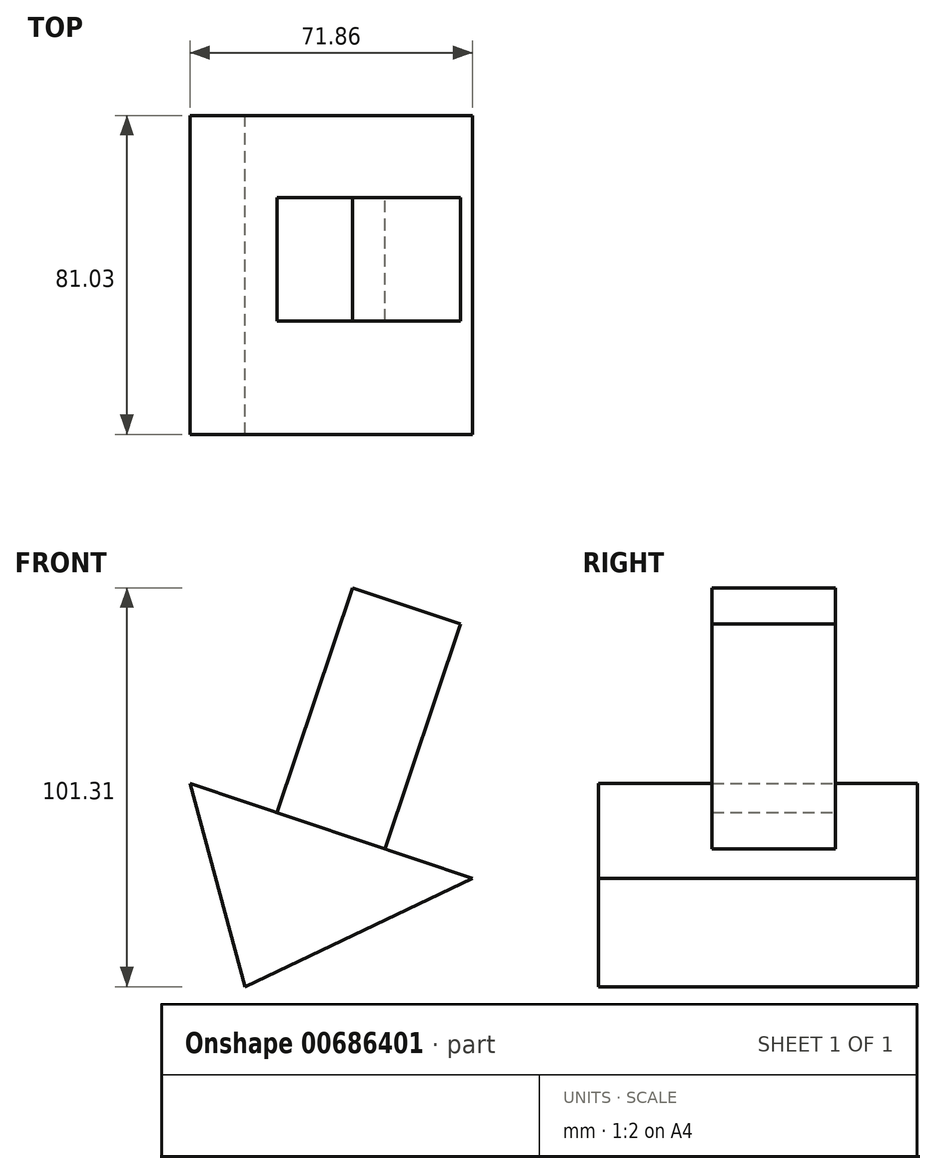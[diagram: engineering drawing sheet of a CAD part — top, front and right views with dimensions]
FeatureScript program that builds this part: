
annotation { "Feature Type Name" : "Feature", "Feature Type Description" : "" }
export const myFeature = defineFeature(function(context is Context, id is Id, definition is map)
    precondition{}
    {
        {
            var Q0;
            Q0=qCreatedBy(makeId("Front.planeOp"),FACE);
            var sketch = newSketch(context, id + "F0", { "sketchPlane" : qUnion([Q0])});
            skLineSegment(sketch, "E0", {"start": v(1.69, 0) * mm, "end": v(59.56, 27.56) * mm});
            skLineSegment(sketch, "E1", {"start": v(59.56, 27.56) * mm, "end": v(-12.3, 51.67) * mm});
            skLineSegment(sketch, "E2", {"start": v(-12.3, 51.67) * mm, "end": v(1.69, 0) * mm});
            skSolve(sketch);
        }
        {
            var Q0;
            Q0=makeQuery(id+"F0.imprint","IMPRINT",FACE,{"disambiguationData":[TD([[makeQuery(id+"F0.imprint","IMPRINT",EDGE,{"derivedFrom":sQuery(id+"F0.wireOp",EDGE,"E0")}),1.0]])]});
            extrude(context, id + "F1", {"entities" : qUnion([Q0]), "depth" : 81.03 * mm, "offsetDistance" : 25.4 * mm});
        }
        {
            var Q0;
            Q0=makeQuery(id+"F1.opExtrude","SWEPT_FACE",FACE,{"disambiguationData":[OSD([sQuery(id+"F0.wireOp",EDGE,"E1")])]});
            var sketch = newSketch(context, id + "F2", { "sketchPlane" : qUnion([Q0])});
            skLineSegment(sketch, "E3.bottom", {"start": v(-4.73, -52.2) * mm, "end": v(24.26, -52.2) * mm});
            skLineSegment(sketch, "E3.top", {"start": v(-4.73, -20.84) * mm, "end": v(24.26, -20.84) * mm});
            skLineSegment(sketch, "E3.left", {"start": v(-4.73, -52.2) * mm, "end": v(-4.73, -20.84) * mm});
            skLineSegment(sketch, "E3.right", {"start": v(24.26, -52.2) * mm, "end": v(24.26, -20.84) * mm});
            skSolve(sketch);
        }
        {
            var Q0;
            Q0=makeQuery(id+"F2.imprint","IMPRINT",FACE,{"disambiguationData":[TD([[makeQuery(id+"F2.imprint","IMPRINT",EDGE,{"derivedFrom":sQuery(id+"F2.wireOp",EDGE,"E3.bottom")}),1.0]])]});
            extrude(context, id + "F3", {"entities" : qUnion([Q0]), "operationType" : NewBodyOperationType.ADD, "depth" : 60.2 * mm, "offsetDistance" : 25.4 * mm});
        }
    });
